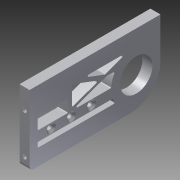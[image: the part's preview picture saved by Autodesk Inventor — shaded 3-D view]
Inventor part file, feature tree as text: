
AUTODESK INVENTOR PART (.ipt)
format: ipt  version: 2015 (Build 190159000, 159)  size: 253,440 bytes
history: native  units: mm
features: sketch x9, extrude x8, projected_geometry x5, hole x3, reference x3, other x2, fillet x2, pattern_linear x1
ambient origin geometry x8: Origin, YZ Plane, XZ Plane, XY Plane, X Axis, Y Axis, Z Axis, Center Point
bodies: Body1 (feature_tree)
feature tree (33):
  other  "Sólido1"
  extrude  "Main Body"  Depth=35.0mm
  extrude  "Bearings"  Depth=20.0mm
  sketch  "Boceto4"  dims[d2=100.0mm d3=0.0mm d11=20.0mm]
  extrude  "Spring_support_space"  Depth=38.0mm
  extrude  "Holes"  Depth=16.1mm
  sketch  "Boceto10"  dims[d30=10.0mm d31=0.0mm d35=2.1mm]
  fillet  "Edges"  Radius=13.0mm
  extrude  "Extrusión6"  Depth=20.0mm
  pattern_linear  "Patrón rectangular1"  Count1=2  [1 undecoded]
  extrude  "Extrusión7"  Depth=35.0mm
  extrude  "Extrusión9"  Depth=10.0mm
  extrude  "Extrusión10"  Depth=15.0mm TaperAngle=0.0deg
  fillet  "Empalme2"  Radius=15.0mm
  sketch  "Boceto13"  dims[d41=6.5mm d42=3.0mm d50=2.4mm d51=33.0mm d52=0.0mm d53=50.0mm d55=13.0mm d56=50.0mm d57=10.0mm d58=0.0mm d59=7.0mm d63=2.0mm d64=2.5mm d65=2.5mm d66=2.0mm d67=2.0mm d68=4.0mm d69=25.0mm d70=5.0mm d71=8.0mm d72=1.0mm d74=1.0mm d75=1.0mm d77=2.0mm d78=10.0mm d79=0.0mm d80=0.5mm d81=3.0mm d82=0.0mm d90=2.4mm d91=6.0mm d92=4.6mm d93=2.0mm d94=90.0deg d95=8.0mm d96=20.594885mm d97=10.0mm d98=10.0mm d99=10.0mm d100=10.0mm d101=2.4mm d102=6.0mm d103=4.6mm d104=2.0mm d105=90.0deg d106=8.0mm d107=20.594885mm d108=10.0mm d109=10.0mm d110=2.4mm d111=6.0mm d112=4.6mm d113=2.0mm d114=90.0deg d115=8.0mm d116=20.594885mm]
  hole  "Agujero4"  [1 undecoded]
  hole  "Agujero5"  [1 undecoded]
  hole  "Agujero6"  [1 undecoded]
  sketch  "Boceto1"  dims[d0=5.0mm d1=35.0mm]
  other  "Axles"
  sketch  "Boceto5"  dims[d12=40.0mm d13=38.0mm]
  sketch  "Boceto6"  dims[d14=20.0mm d22=16.1mm d23=13.0mm]
  sketch  "Boceto7"  dims[d24=100.0mm d25=0.0mm d26=20.0mm d27=20.0mm]
  projected_geometry  "Contorno proyectado2"
  sketch  "Boceto8"  dims[d28=35.0mm d29=35.0mm]
  reference  "Referencia1"
  reference  "Referencia2"
  reference  "Referencia3"
  projected_geometry  "Contorno proyectado3"
  projected_geometry  "Contorno proyectado4"
  sketch  "Boceto11"  dims[d36=20.0mm d37=15.0mm d38=0.0mm d39=15.0mm]
  projected_geometry  "Contorno proyectado5"
  projected_geometry  "Contorno proyectado6"
note: 4 required parameter values undecoded (feature->parameter linkage not recoverable at this tier; creation-order binding heuristic only, values carry confidence <= 0.55)
